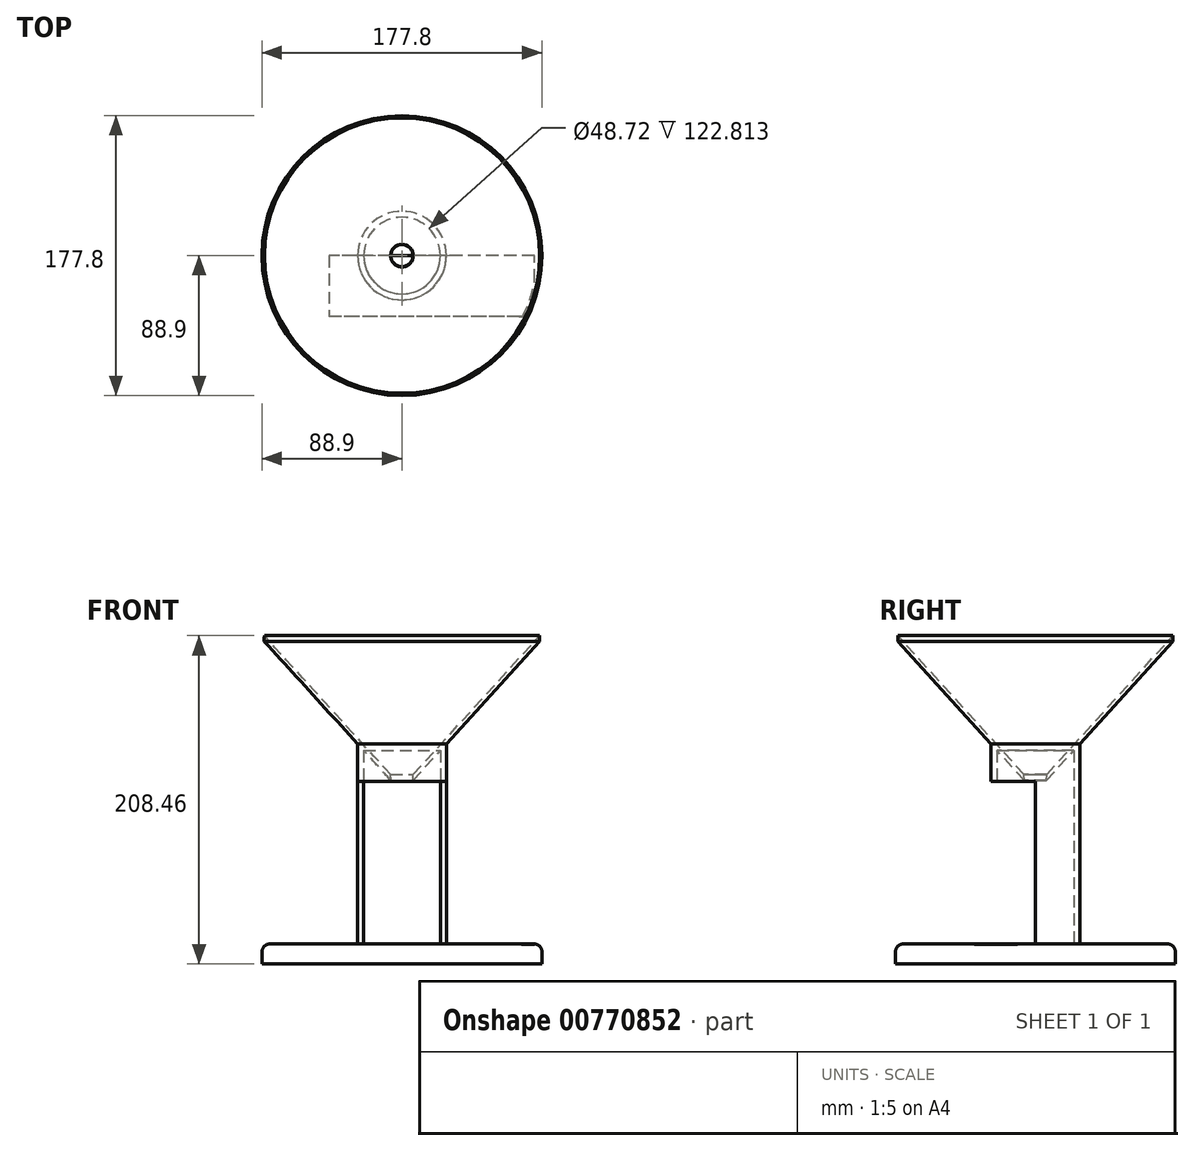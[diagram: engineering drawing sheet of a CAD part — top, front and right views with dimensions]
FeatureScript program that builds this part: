
annotation { "Feature Type Name" : "Feature", "Feature Type Description" : "" }
export const myFeature = defineFeature(function(context is Context, id is Id, definition is map)
    precondition{}
    {
        {
            var Q0;
            Q0=qCreatedBy(makeId("Front.planeOp"),FACE);
            var sketch = newSketch(context, id + "F0", { "sketchPlane" : qUnion([Q0])});
            skLineSegment(sketch, "E0.bottom", {"start": v(-19.05, -113.89) * mm, "end": v(69.85, -113.89) * mm});
            skLineSegment(sketch, "E0.top", {"start": v(-19.05, -101.19) * mm, "end": v(69.85, -101.19) * mm});
            skLineSegment(sketch, "E0.left", {"start": v(-19.05, -113.89) * mm, "end": v(-19.05, -101.19) * mm});
            skLineSegment(sketch, "E0.right", {"start": v(69.85, -113.89) * mm, "end": v(69.85, -101.19) * mm});
            skLineSegment(sketch, "E1", {"start": v(0, 15.8) * mm, "end": v(68.38, 90.93) * mm});
            skLineSegment(sketch, "E2", {"start": v(68.37, 94.57) * mm, "end": v(0, 19.42) * mm});
            skLineSegment(sketch, "E3", {"start": v(68.38, 90.93) * mm, "end": v(68.37, 94.57) * mm});
            skLineSegment(sketch, "E4", {"start": v(9.12, -101.19) * mm, "end": v(9.12, 25.81) * mm});
            skLineSegment(sketch, "E5", {"start": v(5.3, -101.19) * mm, "end": v(5.3, 21.62) * mm});
            skLineSegment(sketch, "E6", {"start": v(0, 15.8) * mm, "end": v(-12.03, 2.57) * mm});
            skLineSegment(sketch, "E7", {"start": v(0, 19.42) * mm, "end": v(-11.88, 6.38) * mm});
            skLineSegment(sketch, "E8", {"start": v(-12.03, 2.57) * mm, "end": v(-11.88, 6.38) * mm});
            skPoint(sketch, "E9.startSnap0", {"position": v(-11.95, 4.48) * mm});
            skSolve(sketch);
        }
        {
            var Q0;
            Q0=makeQuery(id+"F0.imprint","IMPRINT",FACE,{"disambiguationData":[TD([[makeQuery(id+"F0.imprint","IMPRINT",EDGE,{"derivedFrom":sQuery(id+"F0.wireOp",EDGE,"E0.bottom")}),1.0]])]});
            var Q1;
            {var subQ0=sQuery(id+"F0.wireOp",EDGE,"J0ouv3Ya-FSnM-Rf6N-iDuR-PQQUA3BccldQ");Q1=makeQuery(id+"F0.imprint","IMPRINT",FACE,{"disambiguationData":[TD([[makeQuery(id+"F0.imprint","IMPRINT",EDGE,{"derivedFrom":subQ0}),-1.0]])]});}
            var Q2;
            {var subQ0=sQuery(id+"F0.wireOp",EDGE,"E4");Q2=makeQuery(id+"F0.imprint","IMPRINT",FACE,{"disambiguationData":[TD([[makeQuery(id+"F0.imprint","IMPRINT",EDGE,{"derivedFrom":subQ0}),1.0]])]});}
            var Q3;
            {var subQ4=sQuery(id+"F0.wireOp",EDGE,"IBO8bawK-ivg6-STa7-bCEJ-K7RdyAGs7cgW");Q3=makeQuery(id+"F0.imprint","IMPRINT",FACE,{"disambiguationData":[TD([[makeQuery(id+"F0.imprint","IMPRINT",EDGE,{"derivedFrom":subQ4}),-1.0]])]});}
            var Q4;
            Q4=makeQuery(id+"F0.imprint","IMPRINT",FACE,{"disambiguationData":[TD([[makeQuery(id+"F0.imprint","IMPRINT",EDGE,{"derivedFrom":sQuery(id+"F0.wireOp",EDGE,"E2")}),1.0]])]});
            var Q5;
            Q5=sQuery(id+"F0.wireOp",EDGE,"E0.left");
            revolve(context, id + "F1", {"surfaceOperationType" : NewSurfaceOperationType.NEW, "entities" : qUnion([Q0, Q1, Q2, Q3, Q4]), "axis" : qUnion([Q5]), "revolveType" : RevolveType.FULL});
        }
        {
            var Q0;
            Q0=qCreatedBy(makeId("Right.planeOp"),FACE);
            var sketch = newSketch(context, id + "F2", { "sketchPlane" : qUnion([Q0])});
            skLineSegment(sketch, "E10.bottom", {"start": v(-38.74, -101.6) * mm, "end": v(0, -101.6) * mm});
            skLineSegment(sketch, "E10.top", {"start": v(-38.74, 0) * mm, "end": v(0, 0) * mm});
            skLineSegment(sketch, "E10.left", {"start": v(-38.74, -101.6) * mm, "end": v(-38.74, 0) * mm});
            skLineSegment(sketch, "E10.right", {"start": v(0, -101.6) * mm, "end": v(0, 0) * mm});
            skLineSegment(sketch, "E11.top", {"start": v(-38.74, 2.08) * mm, "end": v(0, 2.08) * mm});
            skLineSegment(sketch, "E11.left", {"start": v(-38.74, 0) * mm, "end": v(-38.74, 2.08) * mm});
            skLineSegment(sketch, "E11.right", {"start": v(0, 0) * mm, "end": v(0, 2.08) * mm});
            skSolve(sketch);
        }
        {
            var Q0;
            Q0=makeQuery(id+"F2.imprint","IMPRINT",FACE,{"disambiguationData":[TD([[makeQuery(id+"F2.imprint","IMPRINT",EDGE,{"derivedFrom":sQuery(id+"F2.wireOp",EDGE,"E10.bottom")}),1.0]])]});
            var Q1;
            Q1=makeQuery(id+"F2.imprint","IMPRINT",FACE,{"disambiguationData":[TD([[makeQuery(id+"F2.imprint","IMPRINT",EDGE,{"derivedFrom":sQuery(id+"F2.wireOp",EDGE,"E10.top")}),1.0]])]});
            extrude(context, id + "F3", {"entities" : qUnion([Q0, Q1]), "operationType" : NewBodyOperationType.REMOVE, "endBound" : BoundingType.SYMMETRIC, "depth" : 130.56 * mm, "offsetDistance" : 25.4 * mm});
        }
        {
            var Q0;
            Q0=makeQuery(id+"F1.opRevolve","SWEPT_EDGE",EDGE,{"disambiguationData":[OSD([sQuery(id+"F0.wireOp",EDGE,"E0.top"),sQuery(id+"F0.wireOp",EDGE,"E0.right")])]});
            fillet(context, id + "F4", {"entities" : qUnion([Q0]), "radius" : 5.08 * mm, "allowEdgeOverflow" : false});
        }
    });
